# Revit family: PRD_AR_MxrTps_ThermostaticSingle-leverMixer_F4LT1024
name_source: partatom
category: Plumbing Fixtures
units: mm (PartAtom-declared; Revit-internal decimal feet)

## family parameters
Cut with Voids When Loaded = Yes
Host = Face
OmniClass Number = 23.45.55.17
OmniClass Title = Mixing Faucets
Part Type = Normal
Room Calculation Point = No
Round Connector Dimension = Use Diameter
Shared = No

## types (1)
- F4LT1024
    AccentColour = none
    AssetType = Fixed
    BIMObjectName = PRD_AR_MixerTaps_ThermostaticSingle-leverMixer_F4LT1024
    BasicColour = chrome-look (glossy)
    BodyMaterial = PRD_AR_ChromatedBrass_HighPolished
    Category = Pr_40_20_87_55, Mixer taps
    CloseOffRating = 0.0 Pa
    Color = chrome-look (glossy)
    CompatibleA3000Open = no
    Default Elevation = 1219 mm
    Depressurised = no
    Description = F4LT-Med thermostatic single lever mixer as DN 15 wall-mounted mixer, for wall mounting with lockable swivelling spout, for sanitary facilities in the healthcare and nursing sector, lever length 172 mm.Thermostat-controlled mixer cartridge with expansion element and active scald protection, fail-safe against backflow as well as adjustable, turn-proof temperature stop, ceramic disc technology and flow rate controller 9.0 l/min. Without backflow preventer for optimised drinking water hygiene. Lever cap ergonomically designed in closed construction for contactless lever actuation. For connecting to hot and cold water. Tap optimised for cleaning, scald-protected, safe-touch housing, all-metal construction, polished chromium-plated brass. Decoupled from the tap housing, volume-reduced, smooth water flow from low-lead brass (lead proportion ≤0.2%), and without nickel coating. With thermal insulation components to reduce heat transfer from the tap housing to the cold-water line. Self-emptying spout with laminar jet controller. With adjustable and lockable connections with strainers, fully covered by depth-adjustable screw rosettes. 200 mm projection.
    DiameterNominal = 15  [stored 0.0492126 ft]
    DurationUnit = year
    FaucetFunction = Mixed
    FaucetOperation = LeverHandle
    FaucetType = Pillar
    Features = For connection to hot water and cold water. 200 mm projection.
    Finish = polished chrome-plated
    FlowCoefficient = 0
    FunctionalPrinciple = manual
    IfcExportAs = IfcValveType
    IfcExportType = FAUCET
    InletSize = G 1/2 B
    LockingMechanism = Top section, ceramic
    Manufacturer = KWC Group AG
    ManufacturerName = KWC Group AG
    ManufacturerURL = www.kwc.com
    Material = Brass
    MaterialFitting = brass-look
    MinimumFlowPressure = 1 bar
    Model = F4LT1024
    ModelNumber = 2030072407
    ModelReference = F4LT1024
    NBSDescription = Taps and water supply fittings for sinks
    NBSReference = 45-35-70/345
    Name = F4LT-Med thermostatic single lever mixer F4LT1024
    NominalDepth = 0 mm  [stored 0 ft]
    NominalHeight = 0 mm  [stored 0 ft]
    NominalWidth = 220 mm  [stored 0.721785 ft]
    OverallWidth = 220 mm
    Pop-upWasteSet = no
    ProductInformation = http://pim.kwc.com
    Shape = Bib tap
    Size = 15
    Spout = rotating, bottom
    SpoutProjection = 115 mm
    Status = New
    SurfaceFinishCasing = chromed
    SurfaceFinishFitting = chromed
    SurfaceTreatmentFitting = polished
    TailorMade = no
    TemperatureLimit = yes
    TestPressure = 0.0 Pa
    TypeOfMixing = with thermostat
    TypeOfMounting = wall mounting
    TypeOfOperation = manual operation
    TypeOfTap = bib tap
    URL = www.kwc.com
    Uniclass2015Code = Pr_40_20_87_55
    Uniclass2015Title = Mixer taps
    Uniclass2015Version = Products v1.32
    ValveMechanism = OTHER
    ValveOperation = LEVER
    ValvePattern = STRAIGHT_3_PORT
    Version = 1
    VolumeFlowRate = 0.15 l/s at 3 bar
    WarrantyDurationUnit = year
    WaterConnection = S-unions
    WorkingPressure = 0.0 Pa

note: [stored X ft] marks values corroborated as IEEE doubles in the binary element streams (Revit-internal decimal feet)

## geometry (parser evidence)
native form markers: Sweep x11
no freeform markers — native parametric forms only
